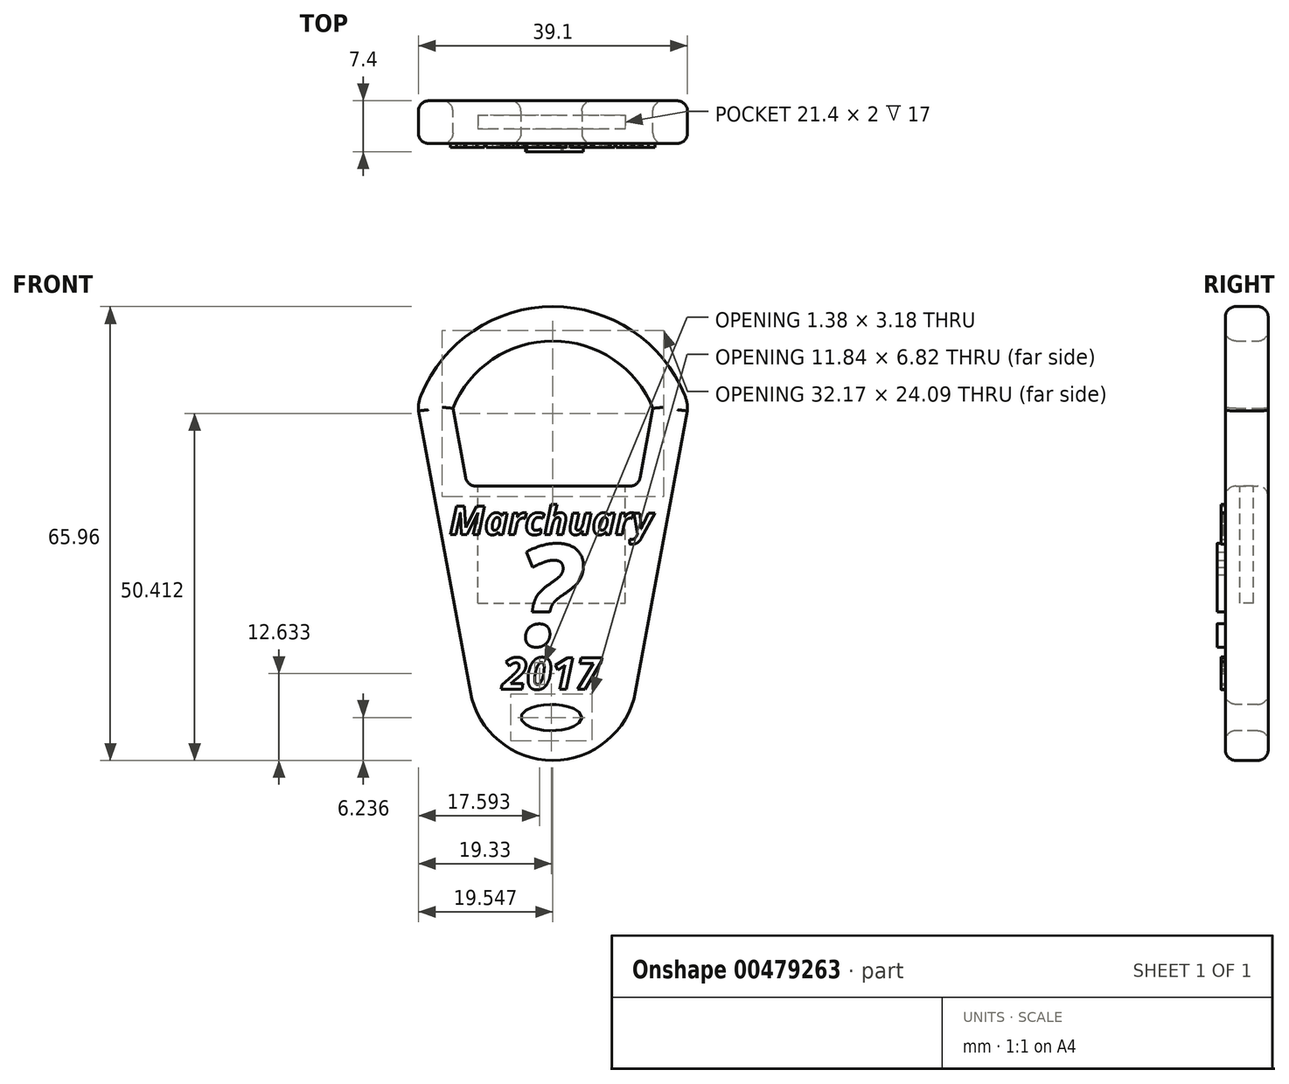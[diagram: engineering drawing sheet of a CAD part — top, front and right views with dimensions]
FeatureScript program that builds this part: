
annotation { "Feature Type Name" : "Feature", "Feature Type Description" : "" }
export const myFeature = defineFeature(function(context is Context, id is Id, definition is map)
    precondition{}
    {
        {
            var Q0;
            Q0=qCreatedBy(makeId("Front.planeOp"),FACE);
            var sketch = newSketch(context, id + "F0", { "sketchPlane" : qUnion([Q0])});
            skLineSegment(sketch, "E0", {"start": v(0.22, 53.5) * mm, "end": v(0.22, -27.22) * mm, "construction": true});
            skLineSegment(sketch, "E1", {"start": v(19.76, 12.33) * mm, "end": v(12.22, -28.48) * mm});
            skLineSegment(sketch, "E2.MirrorCS", {"start": v(-19.33, 12.33) * mm, "end": v(-11.78, -28.48) * mm});
            skLineSegment(sketch, "E3.0", {"start": v(-14.31, 12.71) * mm, "end": v(-12.22, 1.4) * mm});
            skLineSegment(sketch, "E3.3", {"start": v(14.75, 12.71) * mm, "end": v(12.66, 1.4) * mm});
            skLineSegment(sketch, "E4", {"start": v(-12.22, 1.4) * mm, "end": v(12.66, 1.4) * mm});
            skPoint(sketch, "E5", {"position": v(0.22, 20.6) * mm});
            skPoint(sketch, "E6", {"position": v(-14.31, 12.71) * mm});
            skPoint(sketch, "E7.MirrorP", {"position": v(14.75, 12.71) * mm});
            skArc(sketch, "E8", {"start": v(14.75, 12.71) * mm, "mid": v(0.22, 22.5) * mm, "end": v(-14.31, 12.71) * mm});
            skArc(sketch, "E9.0", {"start": v(19.62, 13.97) * mm, "mid": v(0.56, 27.5) * mm, "end": v(-18.94, 14.6) * mm});
            skArc(sketch, "E10", {"start": v(-18.94, 14.6) * mm, "mid": v(-19.26, 13.5) * mm, "end": v(-19.33, 12.33) * mm});
            skArc(sketch, "E11.MirrorCS", {"start": v(19.38, 14.6) * mm, "mid": v(19.7, 13.5) * mm, "end": v(19.76, 12.33) * mm});
            skPoint(sketch, "E12.orphan", {"position": v(-21.9, 26.19) * mm});
            skPoint(sketch, "E13.orphan", {"position": v(22.32, 26.19) * mm});
            skPoint(sketch, "E14.MirrorCS.start.orphan", {"position": v(0.22, 25.6) * mm});
            skArc(sketch, "E15", {"start": v(-11.78, -28.48) * mm, "mid": v(0.22, -38.46) * mm, "end": v(12.22, -28.48) * mm});
            skPoint(sketch, "E16.MirrorCS.end.orphan", {"position": v(0.22, -28.48) * mm});
            skPoint(sketch, "E16.MirrorCS.start.orphan", {"position": v(-11.78, -28.48) * mm});
            skLineSegment(sketch, "E17", {"start": v(-11.78, -28.48) * mm, "end": v(12.22, -28.48) * mm, "construction": true});
            skSolve(sketch);
        }
        {
            var Q0;
            Q0=qSketchRegion(id+"F0",true);
            extrude(context, id + "F1", {"entities" : qUnion([Q0]), "depth" : 6.2 * mm});
        }
        {
            var Q0;
            Q0=makeQuery(id+"F1.opExtrude","CAP_FACE",FACE,{"disambiguationData":[OSD([sQuery(id+"F0.wireOp",EDGE,"E1"),sQuery(id+"F0.wireOp",EDGE,"E2.MirrorCS"),sQuery(id+"F0.wireOp",EDGE,"E3.0"),sQuery(id+"F0.wireOp",EDGE,"E3.3"),sQuery(id+"F0.wireOp",EDGE,"E4"),sQuery(id+"F0.wireOp",EDGE,"E8"),sQuery(id+"F0.wireOp",EDGE,"E9.0"),sQuery(id+"F0.wireOp",EDGE,"E10"),sQuery(id+"F0.wireOp",EDGE,"E11.MirrorCS"),sQuery(id+"F0.wireOp",EDGE,"E15")])],"isStart":false});
            var sketch = newSketch(context, id + "F2", { "sketchPlane" : qUnion([Q0])});
            skEllipse(sketch, "E18", {"center": v(0, -32.22) * mm, "majorRadius": 4.42 * mm, "minorRadius": 1.9 * mm, "majorAxis": v(1, 0)});
            skSolve(sketch);
        }
        {
            var Q0;
            Q0=makeQuery(id+"F2.imprint","IMPRINT",FACE,{"disambiguationData":[TD([[makeQuery(id+"F2.imprint","IMPRINT",EDGE,{"derivedFrom":sQuery(id+"F2.wireOp",EDGE,"E18")}),1.0]])]});
            extrude(context, id + "F3", {"entities" : qUnion([Q0]), "operationType" : NewBodyOperationType.REMOVE, "oppositeDirection" : true, "depth" : 6.5 * mm});
        }
        {
            var Q0;
            Q0=makeQuery(id+"F1.opExtrude","SWEPT_FACE",FACE,{"disambiguationData":[OSD([sQuery(id+"F0.wireOp",EDGE,"E4")])]});
            var sketch = newSketch(context, id + "F4", { "sketchPlane" : qUnion([Q0])});
            skLineSegment(sketch, "E19", {"start": v(0, -2.1) * mm, "end": v(10.7, -2.1) * mm});
            skLineSegment(sketch, "E20.0", {"start": v(0, -4.1) * mm, "end": v(10.7, -4.1) * mm});
            skLineSegment(sketch, "E21", {"start": v(10.7, -2.1) * mm, "end": v(10.7, -4.1) * mm});
            skLineSegment(sketch, "E22", {"start": v(0, -2.1) * mm, "end": v(0, -4.1) * mm, "construction": true});
            skLineSegment(sketch, "E23.MirrorCS", {"start": v(0, -2.1) * mm, "end": v(-10.7, -2.1) * mm});
            skLineSegment(sketch, "E24.MirrorCS", {"start": v(-10.7, -2.1) * mm, "end": v(-10.7, -4.1) * mm});
            skLineSegment(sketch, "E25.MirrorCS", {"start": v(0, -4.1) * mm, "end": v(-10.7, -4.1) * mm});
            skSolve(sketch);
        }
        {
            var Q0;
            Q0=makeQuery(id+"F4.imprint","IMPRINT",FACE,{"disambiguationData":[TD([[makeQuery(id+"F4.imprint","IMPRINT",EDGE,{"derivedFrom":sQuery(id+"F4.wireOp",EDGE,"E19")}),-1.0]])]});
            extrude(context, id + "F5", {"entities" : qUnion([Q0]), "operationType" : NewBodyOperationType.REMOVE, "oppositeDirection" : true, "depth" : 17 * mm});
        }
        {
            var Q0;
            Q0=makeQuery(id+"F1.opExtrude","SWEPT_EDGE",EDGE,{"disambiguationData":[OSD([sQuery(id+"F0.wireOp",EDGE,"E3.0"),sQuery(id+"F0.wireOp",EDGE,"E4")])]});
            var Q1;
            Q1=makeQuery(id+"F1.opExtrude","SWEPT_EDGE",EDGE,{"disambiguationData":[OSD([sQuery(id+"F0.wireOp",EDGE,"E3.3"),sQuery(id+"F0.wireOp",EDGE,"E4")])]});
            var Q2;
            Q2=makeQuery(id+"F1.opExtrude","CAP_FACE",FACE,{"disambiguationData":[OSD([sQuery(id+"F0.wireOp",EDGE,"E1"),sQuery(id+"F0.wireOp",EDGE,"E2.MirrorCS"),sQuery(id+"F0.wireOp",EDGE,"E3.0"),sQuery(id+"F0.wireOp",EDGE,"E3.3"),sQuery(id+"F0.wireOp",EDGE,"E4"),sQuery(id+"F0.wireOp",EDGE,"E8"),sQuery(id+"F0.wireOp",EDGE,"E9.0"),sQuery(id+"F0.wireOp",EDGE,"E10"),sQuery(id+"F0.wireOp",EDGE,"E11.MirrorCS"),sQuery(id+"F0.wireOp",EDGE,"E15")])],"isStart":false});
            var Q3;
            Q3=makeQuery(id+"F1.opExtrude","CAP_FACE",FACE,{"disambiguationData":[OSD([sQuery(id+"F0.wireOp",EDGE,"E1"),sQuery(id+"F0.wireOp",EDGE,"E2.MirrorCS"),sQuery(id+"F0.wireOp",EDGE,"E3.0"),sQuery(id+"F0.wireOp",EDGE,"E3.3"),sQuery(id+"F0.wireOp",EDGE,"E4"),sQuery(id+"F0.wireOp",EDGE,"E8"),sQuery(id+"F0.wireOp",EDGE,"E9.0"),sQuery(id+"F0.wireOp",EDGE,"E10"),sQuery(id+"F0.wireOp",EDGE,"E11.MirrorCS"),sQuery(id+"F0.wireOp",EDGE,"E15")])],"isStart":true});
            fillet(context, id + "F6", {"entities" : qUnion([Q0, Q1, Q2, Q3]), "radius" : 1.5 * mm, "tangentPropagation" : true, "allowEdgeOverflow" : false});
        }
        {
            var Q0;
            Q0=makeQuery(id+"F1.opExtrude","CAP_FACE",FACE,{"disambiguationData":[OSD([sQuery(id+"F0.wireOp",EDGE,"E1"),sQuery(id+"F0.wireOp",EDGE,"E2.MirrorCS"),sQuery(id+"F0.wireOp",EDGE,"E3.0"),sQuery(id+"F0.wireOp",EDGE,"E3.3"),sQuery(id+"F0.wireOp",EDGE,"E4"),sQuery(id+"F0.wireOp",EDGE,"E8"),sQuery(id+"F0.wireOp",EDGE,"E9.0"),sQuery(id+"F0.wireOp",EDGE,"E10"),sQuery(id+"F0.wireOp",EDGE,"E11.MirrorCS"),sQuery(id+"F0.wireOp",EDGE,"E15")])],"isStart":false});
            var sketch = newSketch(context, id + "F7", { "sketchPlane" : qUnion([Q0])});
            skText(sketch, "E26", { "text": "Marchuary", "fontName": "OpenSans-BoldItalic.ttf"});
            const initialGuessF7  = {"E26": [-0.01479, -0.00565, 1, 0, 0.00415]};
            skSetInitialGuess(sketch, initialGuessF7);
            skSolve(sketch);
        }
        {
            var Q0;
            Q0 = qSketchRegion(id + "F7", true);
            extrude(context, id + "F8", {"entities" : qUnion([Q0]), "operationType" : NewBodyOperationType.ADD, "depth" : .6 * mm, "offsetDistance" : 25 * mm});
        }
        {
            var Q0;
            {var subQ4=sQuery(id+"F0.wireOp",EDGE,"E11.MirrorCS");var subQ6=sQuery(id+"F0.wireOp",EDGE,"E2.MirrorCS");var subQ7=sQuery(id+"F0.wireOp",EDGE,"E1");var subQ8=sQuery(id+"F0.wireOp",EDGE,"E4");var subQ9=sQuery(id+"F0.wireOp",EDGE,"E3.3");var subQ10=sQuery(id+"F0.wireOp",EDGE,"E3.0");var subQ11=sQuery(id+"F0.wireOp",EDGE,"E15");var subQ14=sQuery(id+"F0.wireOp",EDGE,"E8");var subQ26=sQuery(id+"F0.wireOp",EDGE,"E9.0");var subQ27=sQuery(id+"F0.wireOp",EDGE,"E10");Q0=makeQuery(id+"F8.boolean.opBoolean","SPLIT",FACE,{"disambiguationData":[TD([makeQuery(id+"F6.opFillet","BLEND_FACE",FACE,{"disambiguationData":[OSD([sQuery(id+"F2.wireOp",EDGE,"E18")])]})])],"derivedFrom":makeQuery(id+"F1.opExtrude","CAP_FACE",FACE,{"disambiguationData":[OSD([subQ7,subQ6,subQ10,subQ9,subQ8,subQ14,subQ26,subQ27,subQ4,subQ11])],"isStart":false})});}
            var sketch = newSketch(context, id + "F9", { "sketchPlane" : qUnion([Q0])});
            skText(sketch, "E27", { "text": "2017", "fontName": "OpenSans-BoldItalic.ttf"});
            const initialGuessF9  = {"E27": [-0.00716, -0.02814, 1, 0, 0.00466]};
            skSetInitialGuess(sketch, initialGuessF9);
            skSolve(sketch);
        }
        {
            var Q0;
            Q0 = qSketchRegion(id + "F9", true);
            extrude(context, id + "F10", {"entities" : qUnion([Q0]), "depth" : .6 * mm, "offsetDistance" : 25 * mm});
        }
        {
            var Q0;
            {var subQ4=sQuery(id+"F0.wireOp",EDGE,"E11.MirrorCS");var subQ6=sQuery(id+"F0.wireOp",EDGE,"E2.MirrorCS");var subQ7=sQuery(id+"F0.wireOp",EDGE,"E1");var subQ8=sQuery(id+"F0.wireOp",EDGE,"E4");var subQ9=sQuery(id+"F0.wireOp",EDGE,"E3.3");var subQ10=sQuery(id+"F0.wireOp",EDGE,"E3.0");var subQ11=sQuery(id+"F0.wireOp",EDGE,"E15");var subQ14=sQuery(id+"F0.wireOp",EDGE,"E8");var subQ26=sQuery(id+"F0.wireOp",EDGE,"E9.0");var subQ27=sQuery(id+"F0.wireOp",EDGE,"E10");Q0=makeQuery(id+"F8.boolean.opBoolean","SPLIT",FACE,{"disambiguationData":[TD([makeQuery(id+"F6.opFillet","BLEND_FACE",FACE,{"disambiguationData":[OSD([sQuery(id+"F2.wireOp",EDGE,"E18")])]})])],"derivedFrom":makeQuery(id+"F1.opExtrude","CAP_FACE",FACE,{"disambiguationData":[OSD([subQ7,subQ6,subQ10,subQ9,subQ8,subQ14,subQ26,subQ27,subQ4,subQ11])],"isStart":false})});}
            var sketch = newSketch(context, id + "F11", { "sketchPlane" : qUnion([Q0])});
            skText(sketch, "E28", { "text": "?", "fontName": "OpenSans-BoldItalic.ttf"});
            const initialGuessF11  = {"E28": [-0.00542, -0.02175, 1, 0, 0.01476]};
            skSetInitialGuess(sketch, initialGuessF11);
            skSolve(sketch);
        }
        {
            var Q0;
            Q0 = qSketchRegion(id + "F11", true);
            extrude(context, id + "F12", {"entities" : qUnion([Q0]), "operationType" : NewBodyOperationType.ADD, "depth" : 1.2 * mm, "offsetDistance" : 25 * mm});
        }
    });
